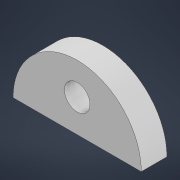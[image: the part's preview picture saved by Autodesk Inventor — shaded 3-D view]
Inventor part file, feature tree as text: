
AUTODESK INVENTOR PART (.ipt)
format: ipt  version: 2022 (Build 260153000, 153)  size: 93,184 bytes
history: native  units: in
note: dims shown in document units (in); Inventor stores cm internally (conversion verified against a paired STEP export)
features: extrude x1, sketch x1
ambient origin geometry x8: Origin, YZ Plane, XZ Plane, XY Plane, X Axis, Y Axis, Z Axis, Center Point
bodies: Solid1 (feature_tree)
feature tree (2):
  extrude  "Extrusion1"  Depth=0.1969in
  sketch  "Sketch1"  dims[d0=0.9843in d1=0.2461in d2=0.1969in d3=0.1969in d4=0.0in]
